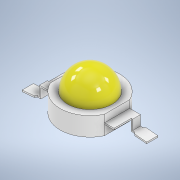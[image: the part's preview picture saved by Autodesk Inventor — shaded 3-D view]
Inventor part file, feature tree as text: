
AUTODESK INVENTOR PART (.ipt)
format: ipt  version: 2020 (Build 240168000, 168)  size: 234,496 bytes
history: native  units: mm
features: sketch x5, extrude x4, projected_geometry x3, revolve x1, pattern_circular x1
ambient origin geometry x8: Origin, YZ Plane, XZ Plane, XY Plane, X Axis, Y Axis, Z Axis, Center Point
bodies: 实体1 (feature_tree)
feature tree (14):
  revolve  "旋转1"  [1 undecoded]
  extrude  "拉伸1"  TaperAngle=90.0deg  [1 undecoded]
  extrude  "拉伸2"  TaperAngle=0.0deg  [1 undecoded]
  extrude  "拉伸3"  Depth=0.2mm TaperAngle=0.0deg
  extrude  "拉伸4"  Depth=1.0mm
  pattern_circular  "环形阵列1"  [2 undecoded]
  sketch  "草图1"  dims[d0=4.0mm d1=2.5mm]
  sketch  "草图2"  dims[d2=3.0mm d3=90.0deg]
  projected_geometry  "投影回路1"
  sketch  "草图3"  dims[d4=3.63mm d5=0.0mm d6=0.0mm]
  sketch  "草图4"  dims[d7=6.0mm d8=0.2mm d9=0.0mm]
  sketch  "草图5"  dims[d10=1.47mm d11=1.0mm d12=0.2mm d13=0.2mm d14=1.5mm d15=0.2mm d16=2.1mm d17=3.8mm d18=0.0mm d19=1.6mm d20=1.5mm d21=45.0deg d22=0.0mm d23=0.0mm d24=20.0mm d25=360.0deg]
  projected_geometry  "投影回路2"
  projected_geometry  "投影回路3"
note: 5 required parameter values undecoded (feature->parameter linkage not recoverable at this tier; creation-order binding heuristic only, values carry confidence <= 0.55)